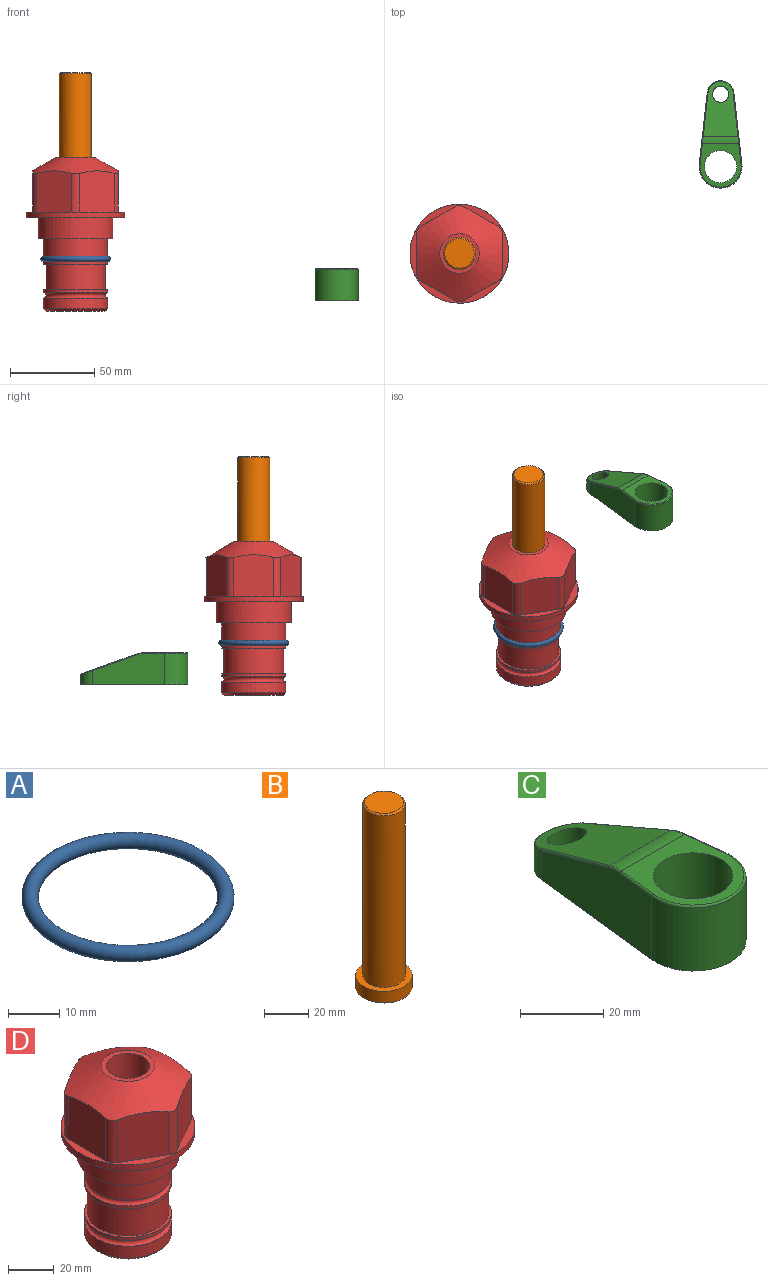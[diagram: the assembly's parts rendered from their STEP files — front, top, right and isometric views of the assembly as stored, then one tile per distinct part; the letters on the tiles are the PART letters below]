
ASSEMBLY  parts=4 mates=1
PART A: 1 faces, bbox 44.7x44.7x3.2 mm
  f0: torus R=19.05mm, axis (0,0,1), area 1193.9mm2
PART B: 6 faces, bbox 25.4x25.4x101.6 mm
  f0: plane 17.46x17.46mm, normal (0,0,1), area 239.5mm2, adj f5
  f1: plane 25.4x25.4mm, normal (0,0,-1), area 506.7mm2, adj f2
  f2: cylinder r=12.7mm len=25.4mm, axis (0,0,1), area 506.7mm2, adj f1,f3
  f3: plane 25.4x25.4mm, normal (0,0,1), area 221.7mm2, adj f2,f4
  f4: cylinder r=9.53mm len=94.46mm, axis (0,0,1), area 5653mm2, adj f3,f5
  f5: cone r=8.73mm half-angle=45deg, axis (0,0,-1), area 64.4mm2, adj f0,f4
PART C: 44 faces, bbox 27.5x64.5x19.1 mm
  f0: plane 2.3x0.95mm, normal (0,0,-1), area 1mm2, adj f25,f30,f34
  f1: plane 63.5x25.4mm, normal (0,0,-1), area 561.7mm2, adj f2,f3,f4,f5,f6,f7,f19,f20
  f2: cylinder r=12.7mm len=25.4mm, axis (0,0,-1), area 792.2mm2, adj f1,f3,f5,f13
  f3: plane 42.33x18.54mm, normal (0.99,0.11,0), area 647mm2, adj f1,f2,f4,f11,f12,f14
  f4: cylinder r=7.94mm len=15.78mm, axis (0,0,-1), area 158.6mm2, adj f1,f3,f5,f16
  f5: plane 42.33x18.54mm, normal (-0.99,0.11,0), area 647mm2, adj f1,f2,f4,f15,f17,f18
  f6: cylinder r=9.53mm len=19.05mm, axis (0,0,-1), area 1140.1mm2, adj f1,f8
  f7: cylinder r=4.76mm len=10.98mm, axis (0,0,-1), area 276.1mm2, adj f1,f9
  f8: plane 25.83x24.38mm, normal (0,0,1), area 262.2mm2, adj f6,f10,f11,f13,f15
  f9: plane 32.49x20.55mm, normal (0,0.34,0.94), area 489.9mm2, adj f7,f10,f14,f16,f18
  f10: cylinder r=12.7mm len=21.49mm, axis (-1,0,0), area 93.2mm2, adj f8,f9,f12,f17
  f11: cylinder r=0.51mm len=12.34mm, axis (0.11,-0.99,0), area 9.9mm2, adj f3,f8,f12,f13
  f12: bspline ~7.62x1.64mm, area 3.5mm2, adj f3,f10,f11,f14
  f13: torus R=12.19mm, axis (0,0,1), area 33.6mm2, adj f2,f8,f11,f15
  f14: cylinder r=0.51mm len=26.01mm, axis (0.1,-0.93,0.34), area 21.6mm2, adj f3,f9,f12,f16
  f15: cylinder r=0.51mm len=12.34mm, axis (0.11,0.99,0), area 9.9mm2, adj f5,f8,f13,f17
  f16: bspline ~15.78x7.05mm, area 15.7mm2, adj f4,f9,f14,f18
  f17: bspline ~7.62x1.64mm, area 3.5mm2, adj f5,f10,f15,f18
  f18: cylinder r=0.51mm len=26.01mm, axis (0.1,0.93,-0.34), area 21.6mm2, adj f5,f9,f16,f17
  f19: plane 21.6x14.29mm, normal (-0.99,-0.11,0), area 242.6mm2, adj f1,f26,f28,f34,f36,f38
  f20: plane 21.6x14.29mm, normal (0.99,-0.11,0), area 242.6mm2, adj f1,f27,f29,f37,f39,f41
  f21: cylinder r=12.7mm len=14.29mm, axis (0,0,-1), area 173.2mm2, adj f1,f26,f27,f30,f31,f33
  f22: cylinder r=7.94mm len=7.63mm, axis (0,0,-1), area 53.8mm2, adj f1,f28,f29,f42
  f23: plane 2.3x0.95mm, normal (0,0,-1), area 1mm2, adj f25,f33,f37
  f24: plane 17.94x12.32mm, normal (0,-0.34,-0.94), area 191.2mm2, adj f25,f38,f41,f42
  f25: cylinder r=9.53mm len=12.93mm, axis (-1,0,0), area 37.5mm2, adj f0,f23,f24,f31,f36,f39
  f26: cylinder r=1.59mm len=14.29mm, axis (0,0,-1), area 49mm2, adj f1,f19,f21,f32
  f27: cylinder r=1.59mm len=14.29mm, axis (0,0,-1), area 49mm2, adj f1,f20,f21,f35
  f28: cylinder r=1.59mm len=7.28mm, axis (0,0,-1), area 22.1mm2, adj f1,f19,f22,f40
  f29: cylinder r=1.59mm len=7.28mm, axis (0,0,-1), area 22.1mm2, adj f1,f20,f22,f43
  f30: torus R=14.29mm, axis (0,0,1), area 5.8mm2, adj f0,f21,f31,f32
  f31: bspline ~11.06x2.73mm, area 20.8mm2, adj f21,f25,f30,f33
  f32: sphere r=1.59mm, area 5.4mm2, adj f26,f30,f34
  f33: torus R=14.29mm, axis (0,0,1), area 5.8mm2, adj f21,f23,f31,f35
  f34: cylinder r=1.59mm len=1.68mm, axis (-0.11,0.99,0), area 2.4mm2, adj f0,f19,f32,f36
  f35: sphere r=1.59mm, area 5.4mm2, adj f27,f33,f37
  f36: bspline ~5.82x2.33mm, area 7.7mm2, adj f19,f25,f34,f38
  f37: cylinder r=1.59mm len=1.68mm, axis (0.11,0.99,0), area 2.4mm2, adj f20,f23,f35,f39
  f38: cylinder r=1.59mm len=18.33mm, axis (0.1,-0.93,0.34), area 46.7mm2, adj f19,f24,f36,f40
  f39: bspline ~5.82x2.33mm, area 7.7mm2, adj f20,f25,f37,f41
  f40: sphere r=1.59mm, area 3.6mm2, adj f28,f38,f42
  f41: cylinder r=1.59mm len=18.33mm, axis (0.1,0.93,-0.34), area 46.7mm2, adj f20,f24,f39,f43
  f42: bspline ~8.31x1.84mm, area 15.3mm2, adj f22,f24,f40,f43
  f43: sphere r=1.59mm, area 3.6mm2, adj f29,f41,f42
PART D: 36 faces, bbox 58.7x58.7x91.2 mm
  f0: cylinder r=17.78mm len=35.56mm, axis (0,0,1), area 1670.8mm2, adj f23,f24,f31
  f1: cylinder r=19.05mm len=38.1mm, axis (0,0,1), area 1191.9mm2, adj f26,f27,f30
  f2: plane 58.66x58.66mm, normal (0,0,-1), area 1150.6mm2, adj f3,f28
  f3: cylinder r=29.33mm len=58.66mm, axis (0,0,-1), area 585.1mm2, adj f2,f4
  f4: plane 58.66x58.66mm, normal (0,0,1), area 475.9mm2, adj f3,f5,f6,f7,f8,f9,f10,f11
  f5: plane 24.5x20.32mm, normal (-0.5,0.87,0), area 562.8mm2, adj f4,f15,f16,f17
  f6: plane 24.5x20.32mm, normal (0.5,0.87,0), area 562.8mm2, adj f4,f14,f15,f17
  f7: plane 24.5x23.48mm, normal (1,0,0), area 562.8mm2, adj f4,f13,f14,f17
  f8: plane 24.5x20.32mm, normal (0.5,-0.87,0), area 562.8mm2, adj f4,f12,f13,f17
  f9: plane 24.5x20.32mm, normal (-0.5,-0.87,0), area 562.8mm2, adj f4,f11,f12,f17
  f10: plane 24.5x23.48mm, normal (-1,0,0), area 562.8mm2, adj f4,f11,f16,f17
  f11: cylinder r=5.08mm len=23.01mm, axis (0,0,-1), area 121.2mm2, adj f4,f9,f10,f17
  f12: cylinder r=5.08mm len=23.01mm, axis (0,0,-1), area 121.2mm2, adj f4,f8,f9,f17
  f13: cylinder r=5.08mm len=23.01mm, axis (0,0,-1), area 121.2mm2, adj f4,f7,f8,f17
  f14: cylinder r=5.08mm len=23.01mm, axis (0,0,-1), area 121.2mm2, adj f4,f6,f7,f17
  f15: cylinder r=5.08mm len=23.01mm, axis (0,0,-1), area 121.2mm2, adj f4,f5,f6,f17
  f16: cylinder r=5.08mm len=23.01mm, axis (0,0,-1), area 121.2mm2, adj f4,f5,f10,f17
  f17: cone r=11.73mm half-angle=60deg, axis (0,0,-1), area 2071.8mm2, adj f5,f6,f7,f8,f9,f10,f11,f12
  f18: plane 23.46x23.46mm, normal (0,0,1), area 147.4mm2, adj f17,f35
  f19: plane 34.93x34.93mm, normal (0,0,-1), area 958mm2, adj f29
  f20: cylinder r=19.05mm len=38.1mm, axis (0,0,1), area 760.1mm2, adj f21,f29
  f21: torus R=19.05mm, axis (0,0,1), area 565.3mm2, adj f20,f22
  f22: cylinder r=19.05mm len=38.1mm, axis (0,0,1), area 190mm2, adj f21,f23
  f23: plane 38.1x38.1mm, normal (0,0,1), area 146.9mm2, adj f0,f22
  f24: plane 38.1x38.1mm, normal (0,0,-1), area 146.9mm2, adj f0,f25
  f25: cylinder r=19.05mm len=38.1mm, axis (0,0,1), area 190mm2, adj f24,f26
  f26: torus R=19.05mm, axis (0,0,1), area 565.3mm2, adj f1,f25
  f27: plane 44.45x44.45mm, normal (0,0,-1), area 411.7mm2, adj f1,f28
  f28: cylinder r=22.23mm len=44.45mm, axis (0,0,1), area 1773.5mm2, adj f2,f27
  f29: cone r=19.05mm half-angle=45deg, axis (0,0,1), area 257.5mm2, adj f19,f20
  f30: cylinder r=3.17mm len=6.75mm, axis (-1,0,0), area 128mm2, adj f1,f33
  f31: cylinder r=3.17mm len=6.35mm, axis (-1,0,0), area 102.5mm2, adj f0,f33
  f32: plane 25.4x25.4mm, normal (0,0,1), area 506.7mm2, adj f33
  f33: cylinder r=12.7mm len=66.42mm, axis (0,0,-1), area 5236.2mm2, adj f30,f31,f32,f34
  f34: cone r=9.53mm half-angle=30deg, axis (0,0,-1), area 443.4mm2, adj f33,f35
  f35: cylinder r=9.53mm len=19.05mm, axis (0,0,-1), area 849mm2, adj f18,f34
PLACE A at identity
PLACE B rot(axis=(0,0,1),13.5deg) t=(0,0,12.19)mm
PLACE C t=(154.67,51.63,-49.38)mm
PLACE D at identity fixed
MATE cylindrical B.f2 <-> D.f0  axis (0,0,1) through (0,0,37.83)mm
